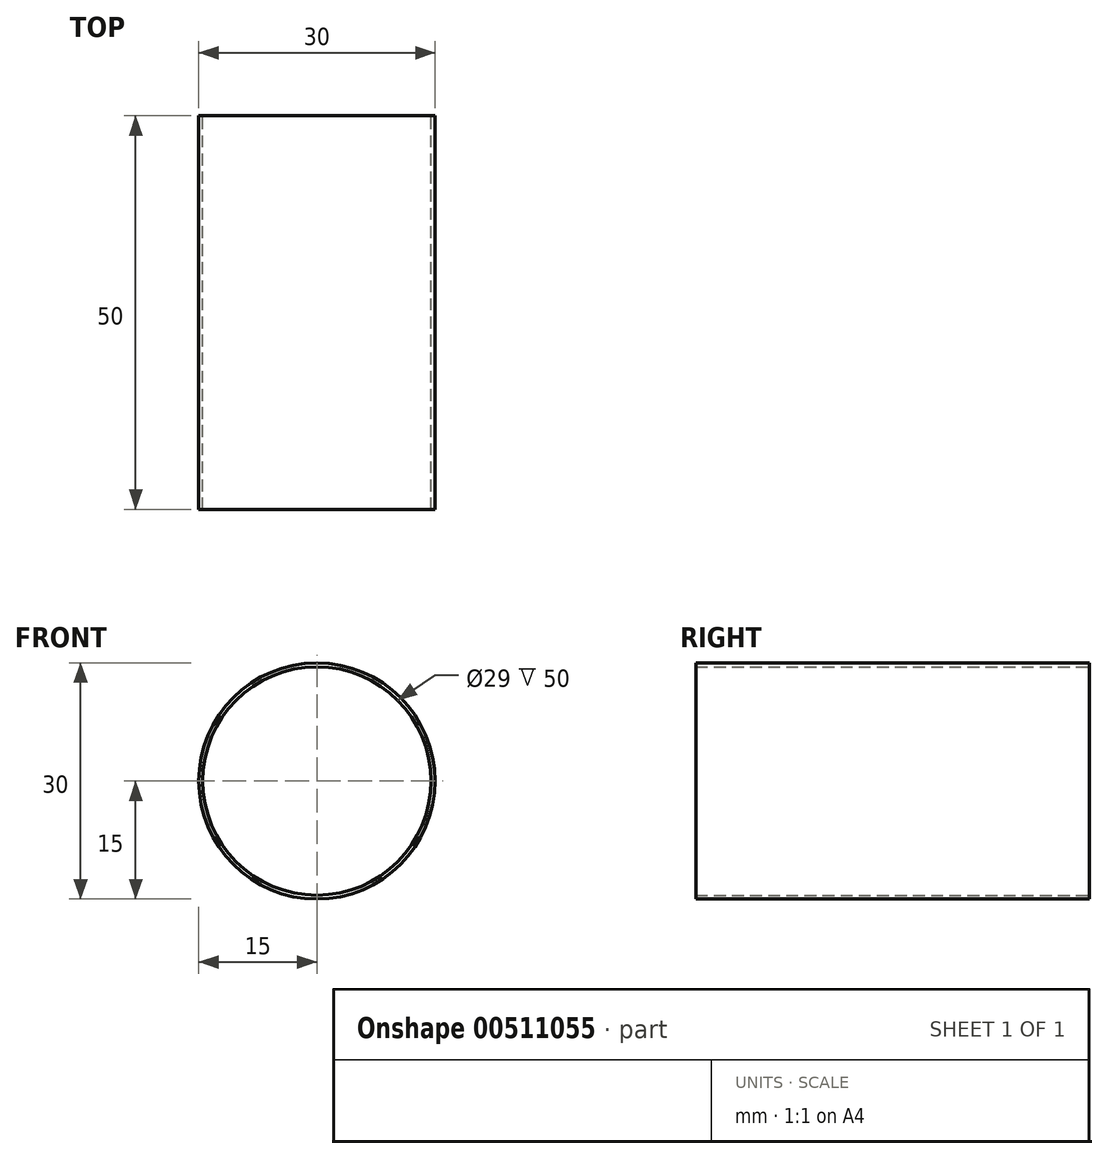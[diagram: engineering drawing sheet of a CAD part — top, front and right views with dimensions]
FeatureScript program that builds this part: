
annotation { "Feature Type Name" : "Feature", "Feature Type Description" : "" }
export const myFeature = defineFeature(function(context is Context, id is Id, definition is map)
    precondition{}
    {
        {
            var Q0;
            Q0=qCreatedBy(makeId("Front.planeOp"),FACE);
            var sketch = newSketch(context, id + "F0", { "sketchPlane" : qUnion([Q0])});
            skCircle(sketch, "E0", {"center": v(0, 0) * mm, "radius": 15 * mm});
            skCircle(sketch, "E1", {"center": v(0, 0) * mm, "radius": 14.5 * mm});
            skSolve(sketch);
        }
        {
            var Q0;
            Q0 = qSketchRegion(id + "F0", true);
            extrude(context, id + "F1", {"entities" : qUnion([Q0]), "depth" : 50 * mm});
        }
    });
